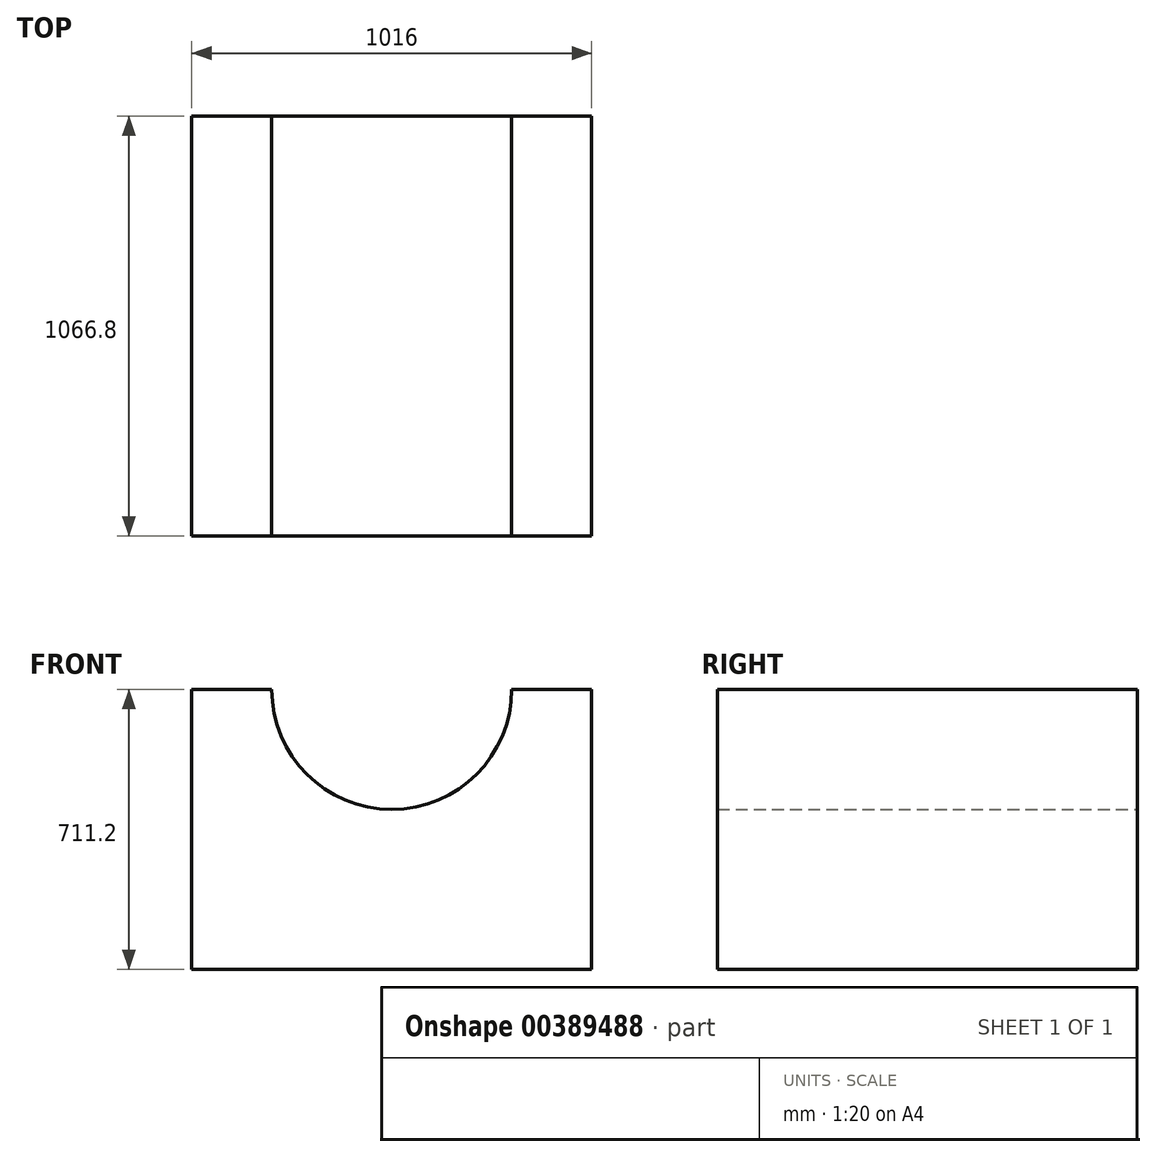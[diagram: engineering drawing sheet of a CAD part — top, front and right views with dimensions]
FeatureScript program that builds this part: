
annotation { "Feature Type Name" : "Feature", "Feature Type Description" : "" }
export const myFeature = defineFeature(function(context is Context, id is Id, definition is map)
    precondition{}
    {
        {
            var Q0;
            Q0=qCreatedBy(makeId("Front.planeOp"),FACE);
            var sketch = newSketch(context, id + "F0", { "sketchPlane" : qUnion([Q0])});
            skLineSegment(sketch, "E0", {"start": v(0, 0) * mm, "end": v(1016, 0) * mm});
            skLineSegment(sketch, "E1", {"start": v(1016, 0) * mm, "end": v(1016, 711.2) * mm});
            skLineSegment(sketch, "E2", {"start": v(1016, 711.2) * mm, "end": v(812.8, 711.2) * mm});
            skLineSegment(sketch, "E3", {"start": v(0, 711.2) * mm, "end": v(0, 0) * mm});
            skArc(sketch, "E4", {"start": v(203.2, 711.2) * mm, "mid": v(508, 406.4) * mm, "end": v(812.8, 711.2) * mm});
            skLineSegment(sketch, "E5.trimOffspring", {"start": v(203.2, 711.2) * mm, "end": v(0, 711.2) * mm});
            skSolve(sketch);
        }
        {
            var Q0;
            Q0 = qSketchRegion(id + "F0", true);
            var Q1;
            Q1=makeQuery(id+"F0.imprint","IMPRINT",FACE,{"disambiguationData":[TD([[makeQuery(id+"F0.imprint","IMPRINT",EDGE,{"derivedFrom":sQuery(id+"F0.wireOp",EDGE,"E0")}),1.0]])]});
            extrude(context, id + "F1", {"entities" : qUnion([Q0, Q1]), "depth" : 1066.8 * mm});
        }
    });
